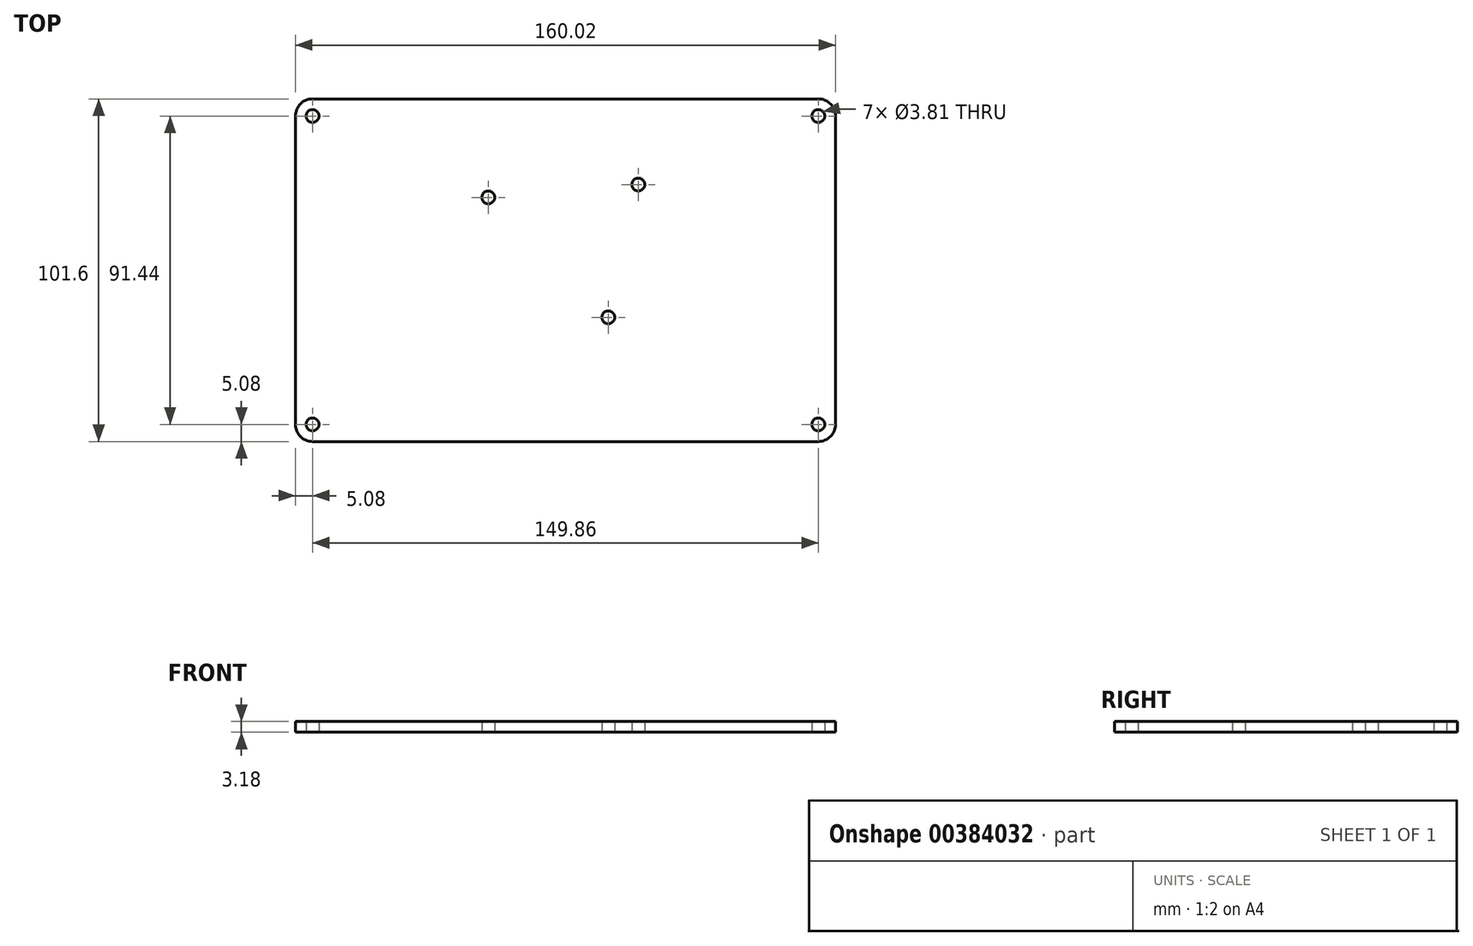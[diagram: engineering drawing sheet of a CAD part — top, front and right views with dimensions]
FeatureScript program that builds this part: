
annotation { "Feature Type Name" : "Feature", "Feature Type Description" : "" }
export const myFeature = defineFeature(function(context is Context, id is Id, definition is map)
    precondition{}
    {
        {
            var Q0;
            Q0=qCreatedBy(makeId("Top.planeOp"),FACE);
            var sketch = newSketch(context, id + "F0", { "sketchPlane" : qUnion([Q0])});
            skLineSegment(sketch, "E0.bottom", {"start": v(-74.93, 50.8) * mm, "end": v(74.93, 50.8) * mm});
            skLineSegment(sketch, "E0.top", {"start": v(-74.93, -50.8) * mm, "end": v(74.93, -50.8) * mm});
            skLineSegment(sketch, "E0.left", {"start": v(-80, 45.72) * mm, "end": v(-80.01, -45.72) * mm});
            skLineSegment(sketch, "E0.right", {"start": v(80.01, 45.72) * mm, "end": v(80.01, -45.72) * mm});
            skCircle(sketch, "E1", {"center": v(-22.86, 21.59) * mm, "radius": 1.9 * mm});
            skCircle(sketch, "E2", {"center": v(21.6, 25.4) * mm, "radius": 1.9 * mm});
            skCircle(sketch, "E3", {"center": v(12.7, -13.97) * mm, "radius": 1.9 * mm});
            skPoint(sketch, "E4.visualSharp", {"position": v(-80, 50.8) * mm});
            skArc(sketch, "E4.filletArc", {"start": v(-74.93, 50.8) * mm, "mid": v(-78.52, 49.31) * mm, "end": v(-80, 45.72) * mm});
            skPoint(sketch, "E5.visualSharp", {"position": v(-80.01, -50.8) * mm});
            skArc(sketch, "E5.filletArc", {"start": v(-80, -45.72) * mm, "mid": v(-78.52, -49.31) * mm, "end": v(-74.93, -50.8) * mm});
            skPoint(sketch, "E6.visualSharp", {"position": v(80, -50.8) * mm});
            skArc(sketch, "E6.filletArc", {"start": v(74.93, -50.8) * mm, "mid": v(78.52, -49.31) * mm, "end": v(80, -45.72) * mm});
            skPoint(sketch, "E7.visualSharp", {"position": v(80, 50.8) * mm});
            skArc(sketch, "E7.filletArc", {"start": v(80.01, 45.72) * mm, "mid": v(78.52, 49.31) * mm, "end": v(74.93, 50.8) * mm});
            skCircle(sketch, "E8", {"center": v(-74.93, 45.72) * mm, "radius": 1.9 * mm});
            skCircle(sketch, "E9", {"center": v(-74.93, -45.72) * mm, "radius": 1.9 * mm});
            skCircle(sketch, "E10", {"center": v(74.93, -45.72) * mm, "radius": 1.9 * mm});
            skCircle(sketch, "E11", {"center": v(74.93, 45.72) * mm, "radius": 1.9 * mm});
            skSolve(sketch);
        }
        {
            var Q0;
            Q0 = qSketchRegion(id + "F0", true);
            extrude(context, id + "F1", {"entities" : qUnion([Q0]), "depth" : 3.17 * mm});
        }
    });
